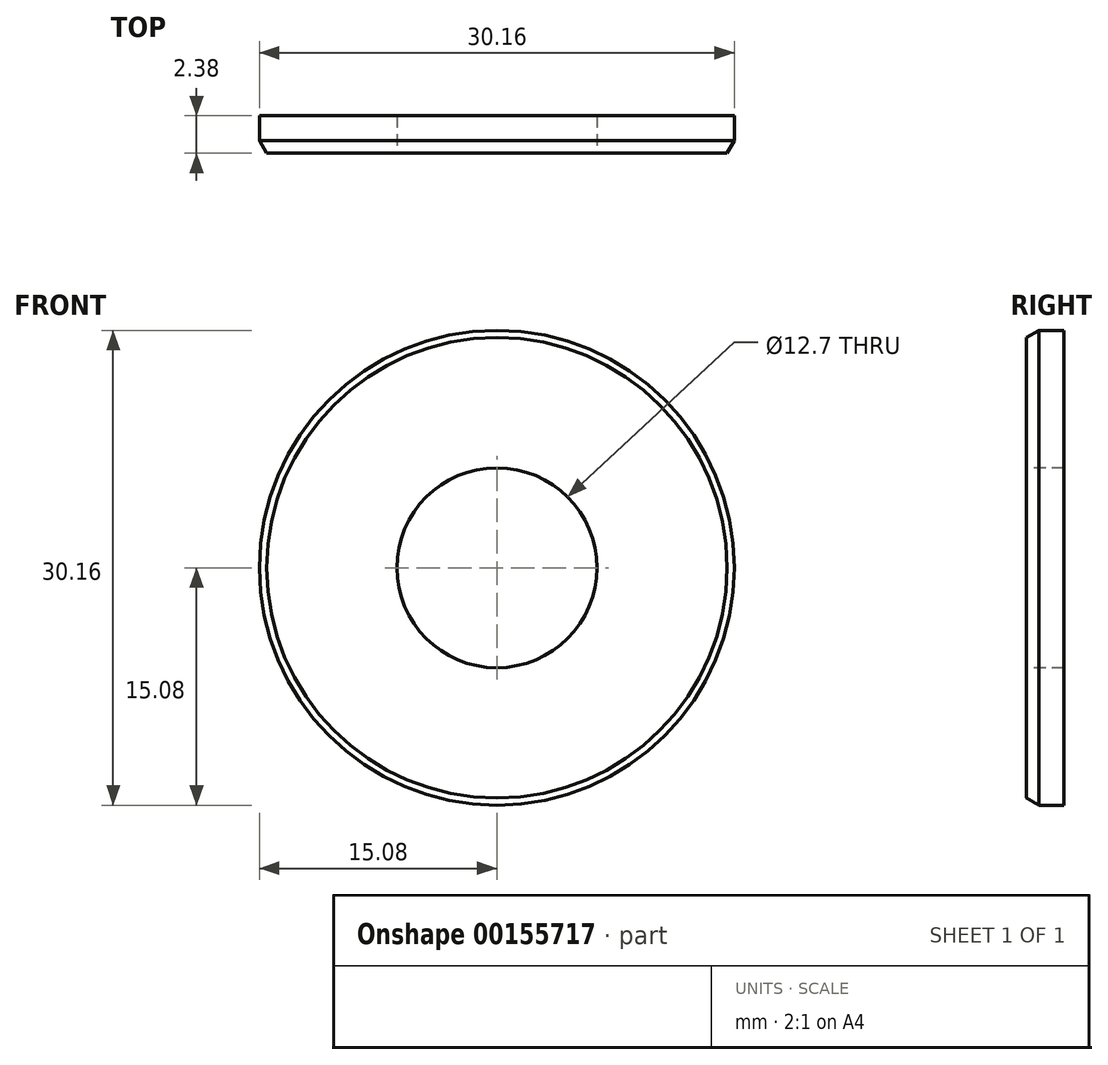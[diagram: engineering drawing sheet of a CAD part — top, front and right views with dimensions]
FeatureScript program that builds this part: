
annotation { "Feature Type Name" : "Feature", "Feature Type Description" : "" }
export const myFeature = defineFeature(function(context is Context, id is Id, definition is map)
    precondition{}
    {
        {
            var Q0;
            Q0=qCreatedBy(makeId("Right.planeOp"),FACE);
            var sketch = newSketch(context, id + "F0", { "sketchPlane" : qUnion([Q0])});
            skLineSegment(sketch, "E0", {"start": v(-1.2, 14.62) * mm, "end": v(-1.2, 6.35) * mm});
            skLineSegment(sketch, "E1", {"start": v(-1.2, 6.35) * mm, "end": v(1.2, 6.35) * mm});
            skLineSegment(sketch, "E2", {"start": v(1.2, 6.35) * mm, "end": v(1.2, 15.08) * mm});
            skLineSegment(sketch, "E3", {"start": v(1.2, 15.08) * mm, "end": v(-0.4, 15.08) * mm});
            skLineSegment(sketch, "E4", {"start": v(-0.4, 15.08) * mm, "end": v(-1.2, 14.62) * mm});
            skLineSegment(sketch, "E5", {"start": v(-7.32, 0) * mm, "end": v(7.71, 0) * mm, "construction": true});
            skSolve(sketch);
        }
        {
            var Q0;
            Q0 = qSketchRegion(id + "F0", true);
            var Q1;
            Q1=sQuery(id+"F0.wireOp",EDGE,"E5");
            revolve(context, id + "F1", {"entities" : qUnion([Q0]), "axis" : qUnion([Q1]), "revolveType" : RevolveType.FULL});
        }
    });
